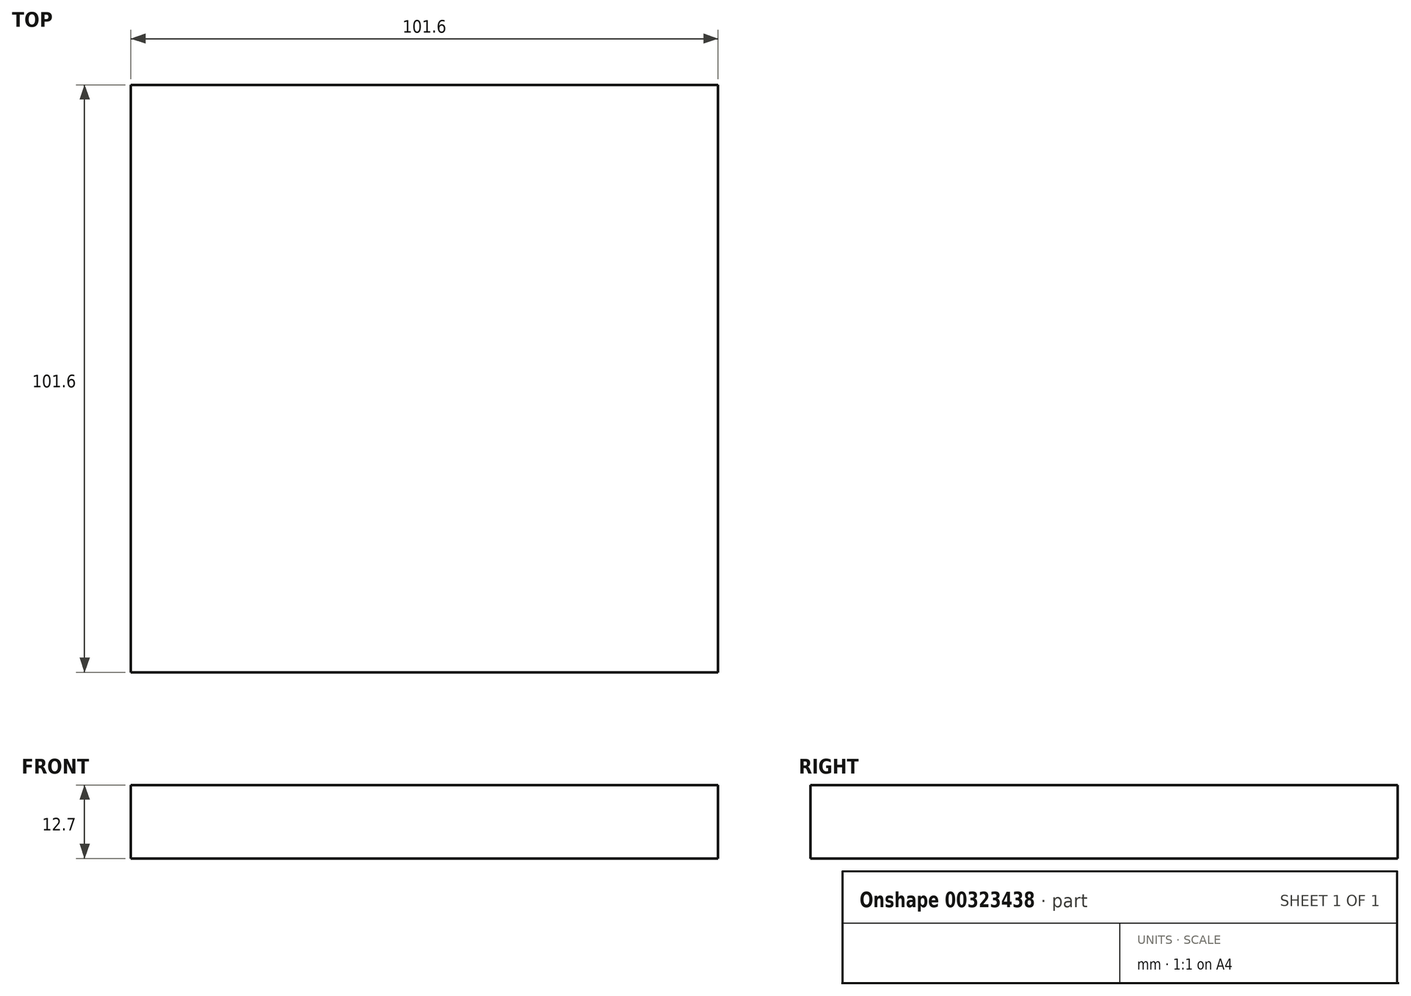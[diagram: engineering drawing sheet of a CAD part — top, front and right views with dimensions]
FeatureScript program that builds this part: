
annotation { "Feature Type Name" : "Feature", "Feature Type Description" : "" }
export const myFeature = defineFeature(function(context is Context, id is Id, definition is map)
    precondition{}
    {
        {
            var Q0;
            Q0=qCreatedBy(makeId("Top.planeOp"),FACE);
            var sketch = newSketch(context, id + "F0", { "sketchPlane" : qUnion([Q0])});
            skLineSegment(sketch, "E0.bottom", {"start": v(0, 0) * mm, "end": v(101.6, 0) * mm});
            skLineSegment(sketch, "E0.top", {"start": v(0, 101.6) * mm, "end": v(101.6, 101.6) * mm});
            skLineSegment(sketch, "E0.left", {"start": v(0, 0) * mm, "end": v(0, 101.6) * mm});
            skLineSegment(sketch, "E0.right", {"start": v(101.6, 0) * mm, "end": v(101.6, 101.6) * mm});
            skSolve(sketch);
        }
        {
            var Q0;
            Q0=makeQuery(id+"F0.imprint","IMPRINT",FACE,{"disambiguationData":[TD([[makeQuery(id+"F0.imprint","IMPRINT",EDGE,{"derivedFrom":sQuery(id+"F0.wireOp",EDGE,"E0.bottom")}),1.0]])]});
            extrude(context, id + "F1", {"entities" : qUnion([Q0]), "depth" : 12.7 * mm});
        }
    });
